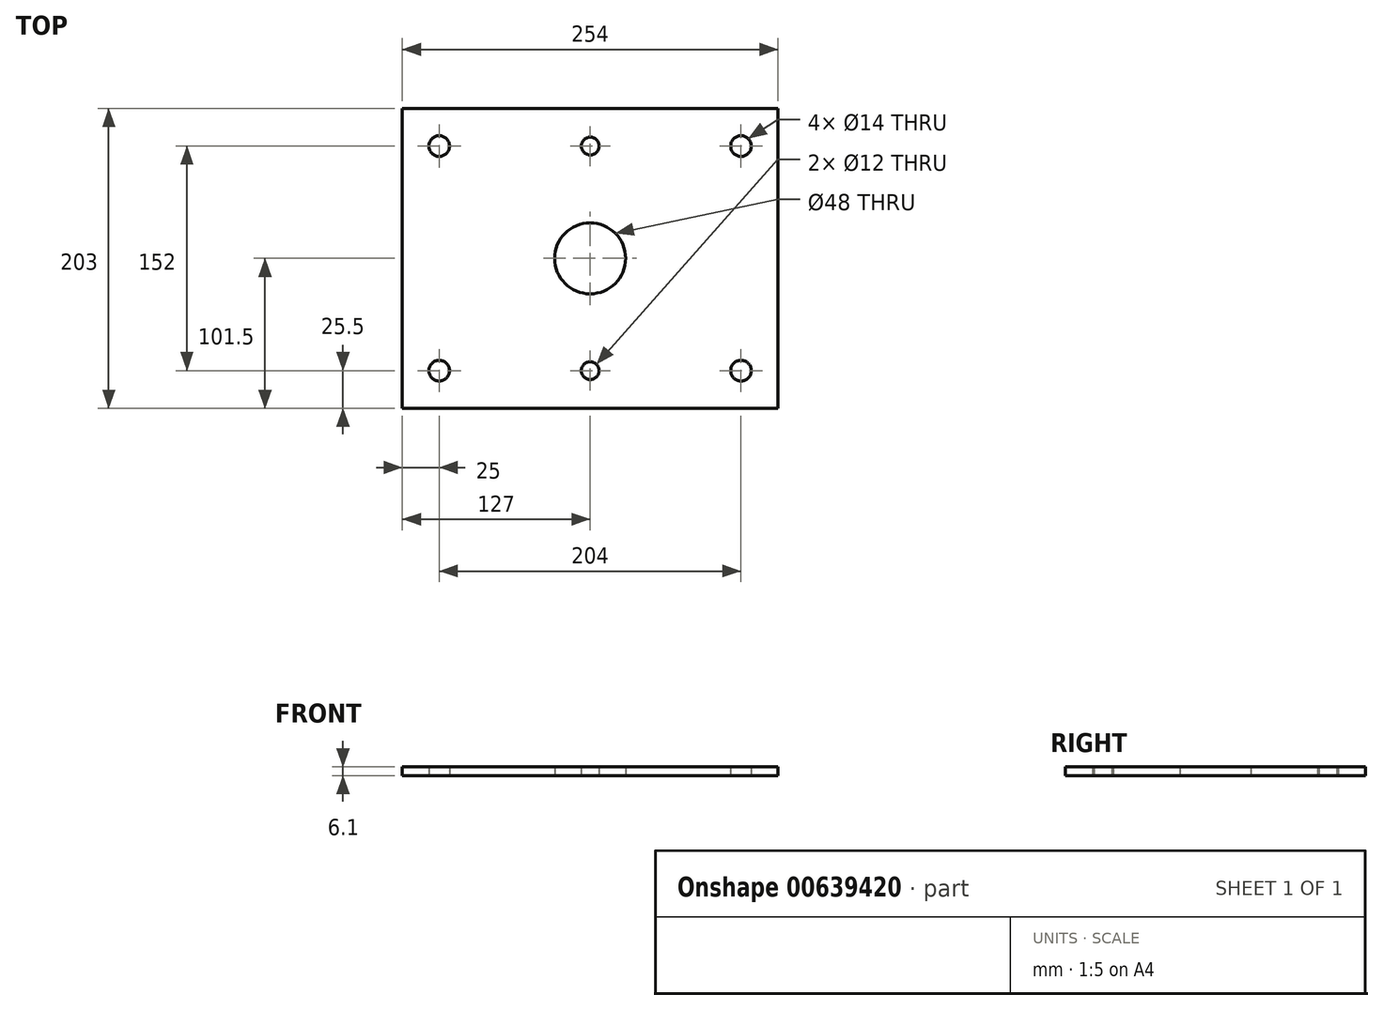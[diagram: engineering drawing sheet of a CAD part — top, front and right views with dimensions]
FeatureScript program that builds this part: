
annotation { "Feature Type Name" : "Feature", "Feature Type Description" : "" }
export const myFeature = defineFeature(function(context is Context, id is Id, definition is map)
    precondition{}
    {
        {
            var Q0;
            Q0=qCreatedBy(makeId("Top.planeOp"),FACE);
            var sketch = newSketch(context, id + "F0", { "sketchPlane" : qUnion([Q0])});
            skLineSegment(sketch, "E0.bottom", {"start": v(0, 0) * mm, "end": v(254, 0) * mm});
            skLineSegment(sketch, "E0.top", {"start": v(0, 203) * mm, "end": v(254, 203) * mm});
            skLineSegment(sketch, "E0.left", {"start": v(0, 0) * mm, "end": v(0, 203) * mm});
            skLineSegment(sketch, "E0.right", {"start": v(254, 0) * mm, "end": v(254, 203) * mm});
            skCircle(sketch, "E1", {"center": v(25, 25.5) * mm, "radius": 7 * mm});
            skPoint(sketch, "E2", {"position": v(127, 0) * mm});
            skPoint(sketch, "E3", {"position": v(0, 101.5) * mm});
            skLineSegment(sketch, "E4", {"start": v(127, 0) * mm, "end": v(127, 203) * mm, "construction": true});
            skLineSegment(sketch, "E5", {"start": v(0, 101.5) * mm, "end": v(254, 101.5) * mm, "construction": true});
            skCircle(sketch, "E6.MirrorC", {"center": v(229, 25.5) * mm, "radius": 7 * mm});
            skCircle(sketch, "E7.MirrorC", {"center": v(25, 177.5) * mm, "radius": 7 * mm});
            skCircle(sketch, "E8.MirrorC", {"center": v(229, 177.5) * mm, "radius": 7 * mm});
            skCircle(sketch, "E9", {"center": v(127, 177.5) * mm, "radius": 6 * mm});
            skCircle(sketch, "E10", {"center": v(127, 25.5) * mm, "radius": 6 * mm});
            skCircle(sketch, "E11", {"center": v(127, 101.5) * mm, "radius": 24 * mm});
            skSolve(sketch);
        }
        {
            var Q0;
            Q0=makeQuery(id+"F0.imprint","IMPRINT",FACE,{"disambiguationData":[TD([[makeQuery(id+"F0.imprint","IMPRINT",EDGE,{"derivedFrom":sQuery(id+"F0.wireOp",EDGE,"E0.bottom")}),1.0]])]});
            extrude(context, id + "F1", {"entities" : qUnion([Q0]), "depth" : 6.1 * mm, "offsetDistance" : 25 * mm});
        }
    });
